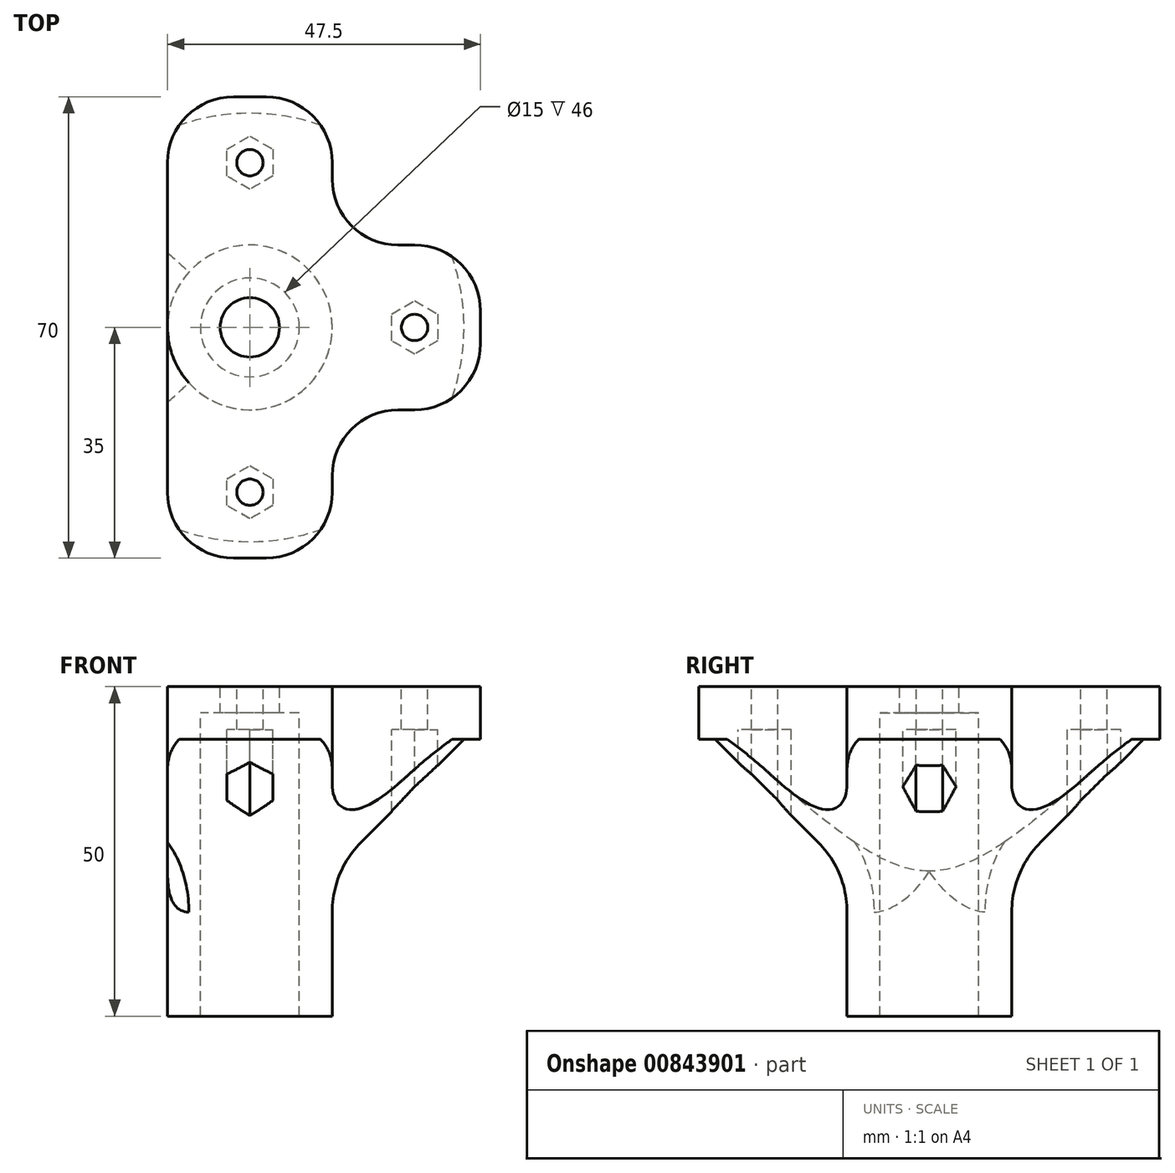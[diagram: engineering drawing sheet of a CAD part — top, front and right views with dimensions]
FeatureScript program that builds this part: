
annotation { "Feature Type Name" : "Feature", "Feature Type Description" : "" }
export const myFeature = defineFeature(function(context is Context, id is Id, definition is map)
    precondition{}
    {
        {
            var Q0;
            Q0=qCreatedBy(makeId("Top.planeOp"),FACE);
            var sketch = newSketch(context, id + "F0", { "sketchPlane" : qUnion([Q0])});
            skCircle(sketch, "E0", {"center": v(0, 0) * mm, "radius": 4.5 * mm});
            skCircle(sketch, "E1", {"center": v(0, 0) * mm, "radius": 7.5 * mm});
            skCircle(sketch, "E2", {"center": v(0, 0) * mm, "radius": 12.5 * mm});
            skLineSegment(sketch, "E3.0", {"start": v(35, 12.5) * mm, "end": v(35, -12.5) * mm});
            skLineSegment(sketch, "E3.1", {"start": v(12.5, -35) * mm, "end": v(-12.5, -35) * mm});
            skLineSegment(sketch, "E3.3", {"start": v(-12.5, 35) * mm, "end": v(12.5, 35) * mm});
            skLineSegment(sketch, "E4", {"start": v(12.5, 12.5) * mm, "end": v(35, 12.5) * mm});
            skLineSegment(sketch, "E5", {"start": v(12.5, -12.5) * mm, "end": v(35, -12.5) * mm});
            skLineSegment(sketch, "E6", {"start": v(-12.5, 0) * mm, "end": v(-12.5, 35) * mm});
            skLineSegment(sketch, "E7", {"start": v(12.5, 12.5) * mm, "end": v(12.5, 35) * mm});
            skLineSegment(sketch, "E8", {"start": v(-12.5, 0) * mm, "end": v(-12.5, -35) * mm});
            skLineSegment(sketch, "E9", {"start": v(12.5, -12.5) * mm, "end": v(12.5, -35) * mm});
            skPoint(sketch, "E10.orphan", {"position": v(12.5, 0) * mm});
            skPoint(sketch, "E11.orphan", {"position": v(0, 12.5) * mm});
            skCircle(sketch, "E12", {"center": v(0, 25) * mm, "radius": 2 * mm});
            skCircle(sketch, "E13.cCircle", {"center": v(0, 25) * mm, "radius": 3.5 * mm, "construction": true});
            skLineSegment(sketch, "E13.0", {"start": v(3.5, 27.02) * mm, "end": v(3.5, 22.98) * mm});
            skLineSegment(sketch, "E13.1", {"start": v(3.5, 22.98) * mm, "end": v(0, 20.96) * mm});
            skLineSegment(sketch, "E13.2", {"start": v(0, 20.96) * mm, "end": v(-3.5, 22.98) * mm});
            skLineSegment(sketch, "E13.3", {"start": v(-3.5, 22.98) * mm, "end": v(-3.5, 27.02) * mm});
            skLineSegment(sketch, "E13.4", {"start": v(-3.5, 27.02) * mm, "end": v(0, 29.04) * mm});
            skLineSegment(sketch, "E13.5", {"start": v(0, 29.04) * mm, "end": v(3.5, 27.02) * mm});
            skPoint(sketch, "E13.0.midPoint", {"position": v(3.5, 25) * mm});
            skCircle(sketch, "E14", {"center": v(0, -25) * mm, "radius": 2 * mm});
            skCircle(sketch, "E15.cCircle", {"center": v(0, -25) * mm, "radius": 3.5 * mm, "construction": true});
            skLineSegment(sketch, "E15.0", {"start": v(3.5, -22.98) * mm, "end": v(3.5, -27.02) * mm});
            skLineSegment(sketch, "E15.1", {"start": v(3.5, -27.02) * mm, "end": v(0, -29.04) * mm});
            skLineSegment(sketch, "E15.2", {"start": v(0, -29.04) * mm, "end": v(-3.5, -27.02) * mm});
            skLineSegment(sketch, "E15.3", {"start": v(-3.5, -27.02) * mm, "end": v(-3.5, -22.98) * mm});
            skLineSegment(sketch, "E15.4", {"start": v(-3.5, -22.98) * mm, "end": v(0, -20.96) * mm});
            skLineSegment(sketch, "E15.5", {"start": v(0, -20.96) * mm, "end": v(3.5, -22.98) * mm});
            skPoint(sketch, "E15.0.midPoint", {"position": v(3.5, -25) * mm});
            skCircle(sketch, "E16.cCircle", {"center": v(25, 0) * mm, "radius": 3.5 * mm, "construction": true});
            skLineSegment(sketch, "E16.0", {"start": v(28.5, 2.02) * mm, "end": v(28.5, -2.02) * mm});
            skLineSegment(sketch, "E16.1", {"start": v(28.5, -2.02) * mm, "end": v(25, -4.04) * mm});
            skLineSegment(sketch, "E16.2", {"start": v(25, -4.04) * mm, "end": v(21.5, -2.02) * mm});
            skLineSegment(sketch, "E16.3", {"start": v(21.5, -2.02) * mm, "end": v(21.5, 2.02) * mm});
            skLineSegment(sketch, "E16.4", {"start": v(21.5, 2.02) * mm, "end": v(25, 4.04) * mm});
            skLineSegment(sketch, "E16.5", {"start": v(25, 4.04) * mm, "end": v(28.5, 2.02) * mm});
            skPoint(sketch, "E16.0.midPoint", {"position": v(28.5, 0) * mm});
            skCircle(sketch, "E17", {"center": v(25, 0) * mm, "radius": 2 * mm});
            skSolve(sketch);
        }
        {
            var Q0;
            Q0 = qSketchRegion(id + "F0", true);
            extrude(context, id + "F1", {"entities" : qUnion([Q0]), "oppositeDirection" : true, "depth" : 8 * mm, "offsetDistance" : 25 * mm});
        }
        {
            var Q0;
            Q0=makeQuery(id+"F0.imprint","IMPRINT",FACE,{"disambiguationData":[TD([[makeQuery(id+"F0.imprint","IMPRINT",EDGE,{"derivedFrom":sQuery(id+"F0.wireOp",EDGE,"E0")}),-1.0]])]});
            extrude(context, id + "F2", {"entities" : qUnion([Q0]), "operationType" : NewBodyOperationType.ADD, "oppositeDirection" : true, "depth" : 4 * mm, "offsetDistance" : 25 * mm});
        }
        {
            var Q0;
            Q0=makeQuery(id+"F0.imprint","IMPRINT",FACE,{"disambiguationData":[TD([[makeQuery(id+"F0.imprint","IMPRINT",EDGE,{"derivedFrom":sQuery(id+"F0.wireOp",EDGE,"E14")}),-1.0]])]});
            var Q1;
            Q1=makeQuery(id+"F0.imprint","IMPRINT",FACE,{"disambiguationData":[TD([[makeQuery(id+"F0.imprint","IMPRINT",EDGE,{"derivedFrom":sQuery(id+"F0.wireOp",EDGE,"E12")}),-1.0]])]});
            var Q2;
            Q2=makeQuery(id+"F0.imprint","IMPRINT",FACE,{"disambiguationData":[TD([[makeQuery(id+"F0.imprint","IMPRINT",EDGE,{"derivedFrom":sQuery(id+"F0.wireOp",EDGE,"E16.0")}),-1.0]])]});
            extrude(context, id + "F3", {"entities" : qUnion([Q0, Q1, Q2]), "operationType" : NewBodyOperationType.ADD, "oppositeDirection" : true, "depth" : (15 - 3.5 - 5) * mm, "offsetDistance" : 25 * mm});
        }
        {
            var Q0;
            Q0=makeQuery(id+"F0.imprint","IMPRINT",FACE,{"disambiguationData":[TD([[makeQuery(id+"F0.imprint","IMPRINT",EDGE,{"derivedFrom":sQuery(id+"F0.wireOp",EDGE,"E1")}),-1.0]])]});
            extrude(context, id + "F4", {"entities" : qUnion([Q0]), "operationType" : NewBodyOperationType.ADD, "oppositeDirection" : true, "depth" : 50 * mm, "offsetDistance" : 25 * mm});
        }
        {
            var Q0;
            Q0=makeQuery(id+"F4.boolean.opBoolean","INTERSECT",EDGE,{"derivedFrom":[makeQuery(id+"F1.opExtrude","CAP_FACE",FACE,{"disambiguationData":[OSD([sQuery(id+"F0.wireOp",EDGE,"E1"),sQuery(id+"F0.wireOp",EDGE,"E3.0"),sQuery(id+"F0.wireOp",EDGE,"E3.1"),sQuery(id+"F0.wireOp",EDGE,"E3.3"),sQuery(id+"F0.wireOp",EDGE,"E4"),sQuery(id+"F0.wireOp",EDGE,"E5"),sQuery(id+"F0.wireOp",EDGE,"E6"),sQuery(id+"F0.wireOp",EDGE,"E7"),sQuery(id+"F0.wireOp",EDGE,"E8"),sQuery(id+"F0.wireOp",EDGE,"E9"),sQuery(id+"F0.wireOp",EDGE,"E13.0"),sQuery(id+"F0.wireOp",EDGE,"E13.1"),sQuery(id+"F0.wireOp",EDGE,"E13.2"),sQuery(id+"F0.wireOp",EDGE,"E13.3"),sQuery(id+"F0.wireOp",EDGE,"E13.4"),sQuery(id+"F0.wireOp",EDGE,"E13.5"),sQuery(id+"F0.wireOp",EDGE,"E15.0"),sQuery(id+"F0.wireOp",EDGE,"E15.1"),sQuery(id+"F0.wireOp",EDGE,"E15.2"),sQuery(id+"F0.wireOp",EDGE,"E15.3"),sQuery(id+"F0.wireOp",EDGE,"E15.4"),sQuery(id+"F0.wireOp",EDGE,"E15.5"),sQuery(id+"F0.wireOp",EDGE,"E16.0"),sQuery(id+"F0.wireOp",EDGE,"E16.1"),sQuery(id+"F0.wireOp",EDGE,"E16.2"),sQuery(id+"F0.wireOp",EDGE,"E16.3"),sQuery(id+"F0.wireOp",EDGE,"E16.4"),sQuery(id+"F0.wireOp",EDGE,"E16.5")])],"isStart":false}),makeQuery(id+"F4.opExtrude","SWEPT_FACE",FACE,{"disambiguationData":[OSD([sQuery(id+"F0.wireOp",EDGE,"E2")])]})]});
            chamfer(context, id + "F5", {"entities" : qUnion([Q0]), "width" : 20 * mm});
        }
        {
            var Q0;
            Q0=makeQuery(id+"F1.opExtrude","SWEPT_EDGE",EDGE,{"disambiguationData":[OSD([sQuery(id+"F0.wireOp",EDGE,"E4"),sQuery(id+"F0.wireOp",EDGE,"E7")])]});
            var Q1;
            Q1=makeQuery(id+"F1.opExtrude","SWEPT_EDGE",EDGE,{"disambiguationData":[OSD([sQuery(id+"F0.wireOp",EDGE,"E3.3"),sQuery(id+"F0.wireOp",EDGE,"E7")])]});
            var Q2;
            Q2=makeQuery(id+"F1.opExtrude","SWEPT_EDGE",EDGE,{"disambiguationData":[OSD([sQuery(id+"F0.wireOp",EDGE,"E3.3"),sQuery(id+"F0.wireOp",EDGE,"E6")])]});
            var Q3;
            Q3=makeQuery(id+"F1.opExtrude","SWEPT_EDGE",EDGE,{"disambiguationData":[OSD([sQuery(id+"F0.wireOp",EDGE,"E3.1"),sQuery(id+"F0.wireOp",EDGE,"E8")])]});
            var Q4;
            Q4=makeQuery(id+"F1.opExtrude","SWEPT_EDGE",EDGE,{"disambiguationData":[OSD([sQuery(id+"F0.wireOp",EDGE,"E3.1"),sQuery(id+"F0.wireOp",EDGE,"E9")])]});
            var Q5;
            Q5=makeQuery(id+"F1.opExtrude","SWEPT_EDGE",EDGE,{"disambiguationData":[OSD([sQuery(id+"F0.wireOp",EDGE,"E5"),sQuery(id+"F0.wireOp",EDGE,"E9")])]});
            var Q6;
            Q6=makeQuery(id+"F1.opExtrude","SWEPT_EDGE",EDGE,{"disambiguationData":[OSD([sQuery(id+"F0.wireOp",EDGE,"E3.0"),sQuery(id+"F0.wireOp",EDGE,"E5")])]});
            var Q7;
            Q7=makeQuery(id+"F1.opExtrude","SWEPT_EDGE",EDGE,{"disambiguationData":[OSD([sQuery(id+"F0.wireOp",EDGE,"E3.0"),sQuery(id+"F0.wireOp",EDGE,"E4")])]});
            fillet(context, id + "F6", {"entities" : qUnion([Q0, Q1, Q2, Q3, Q4, Q5, Q6, Q7]), "radius" : 10 * mm, "tangentPropagation" : true, "allowEdgeOverflow" : false});
        }
        {
            var Q0;
            {var subQ0=makeQuery(id+"F4.opExtrude","SWEPT_FACE",FACE,{"disambiguationData":[OSD([sQuery(id+"F0.wireOp",EDGE,"E2")])]});Q0=makeQuery(id+"F5.opChamfer","BLEND_EDGE",EDGE,{"blendedFrom":[makeQuery(id+"F4.boolean.opBoolean","INTERSECT",EDGE,{"derivedFrom":[makeQuery(id+"F1.opExtrude","CAP_FACE",FACE,{"disambiguationData":[OSD([sQuery(id+"F0.wireOp",EDGE,"E1"),sQuery(id+"F0.wireOp",EDGE,"E3.0"),sQuery(id+"F0.wireOp",EDGE,"E3.1"),sQuery(id+"F0.wireOp",EDGE,"E3.3"),sQuery(id+"F0.wireOp",EDGE,"E4"),sQuery(id+"F0.wireOp",EDGE,"E5"),sQuery(id+"F0.wireOp",EDGE,"E6"),sQuery(id+"F0.wireOp",EDGE,"E7"),sQuery(id+"F0.wireOp",EDGE,"E8"),sQuery(id+"F0.wireOp",EDGE,"E9"),sQuery(id+"F0.wireOp",EDGE,"E13.0"),sQuery(id+"F0.wireOp",EDGE,"E13.1"),sQuery(id+"F0.wireOp",EDGE,"E13.2"),sQuery(id+"F0.wireOp",EDGE,"E13.3"),sQuery(id+"F0.wireOp",EDGE,"E13.4"),sQuery(id+"F0.wireOp",EDGE,"E13.5"),sQuery(id+"F0.wireOp",EDGE,"E15.0"),sQuery(id+"F0.wireOp",EDGE,"E15.1"),sQuery(id+"F0.wireOp",EDGE,"E15.2"),sQuery(id+"F0.wireOp",EDGE,"E15.3"),sQuery(id+"F0.wireOp",EDGE,"E15.4"),sQuery(id+"F0.wireOp",EDGE,"E15.5"),sQuery(id+"F0.wireOp",EDGE,"E16.0"),sQuery(id+"F0.wireOp",EDGE,"E16.1"),sQuery(id+"F0.wireOp",EDGE,"E16.2"),sQuery(id+"F0.wireOp",EDGE,"E16.3"),sQuery(id+"F0.wireOp",EDGE,"E16.4"),sQuery(id+"F0.wireOp",EDGE,"E16.5")])],"isStart":false}),subQ0]}),subQ0],"blendedInto":[subQ0]});}
            fillet(context, id + "F7", {"entities" : qUnion([Q0]), "radius" : 15 * mm, "tangentPropagation" : true, "allowEdgeOverflow" : false});
        }
    });
